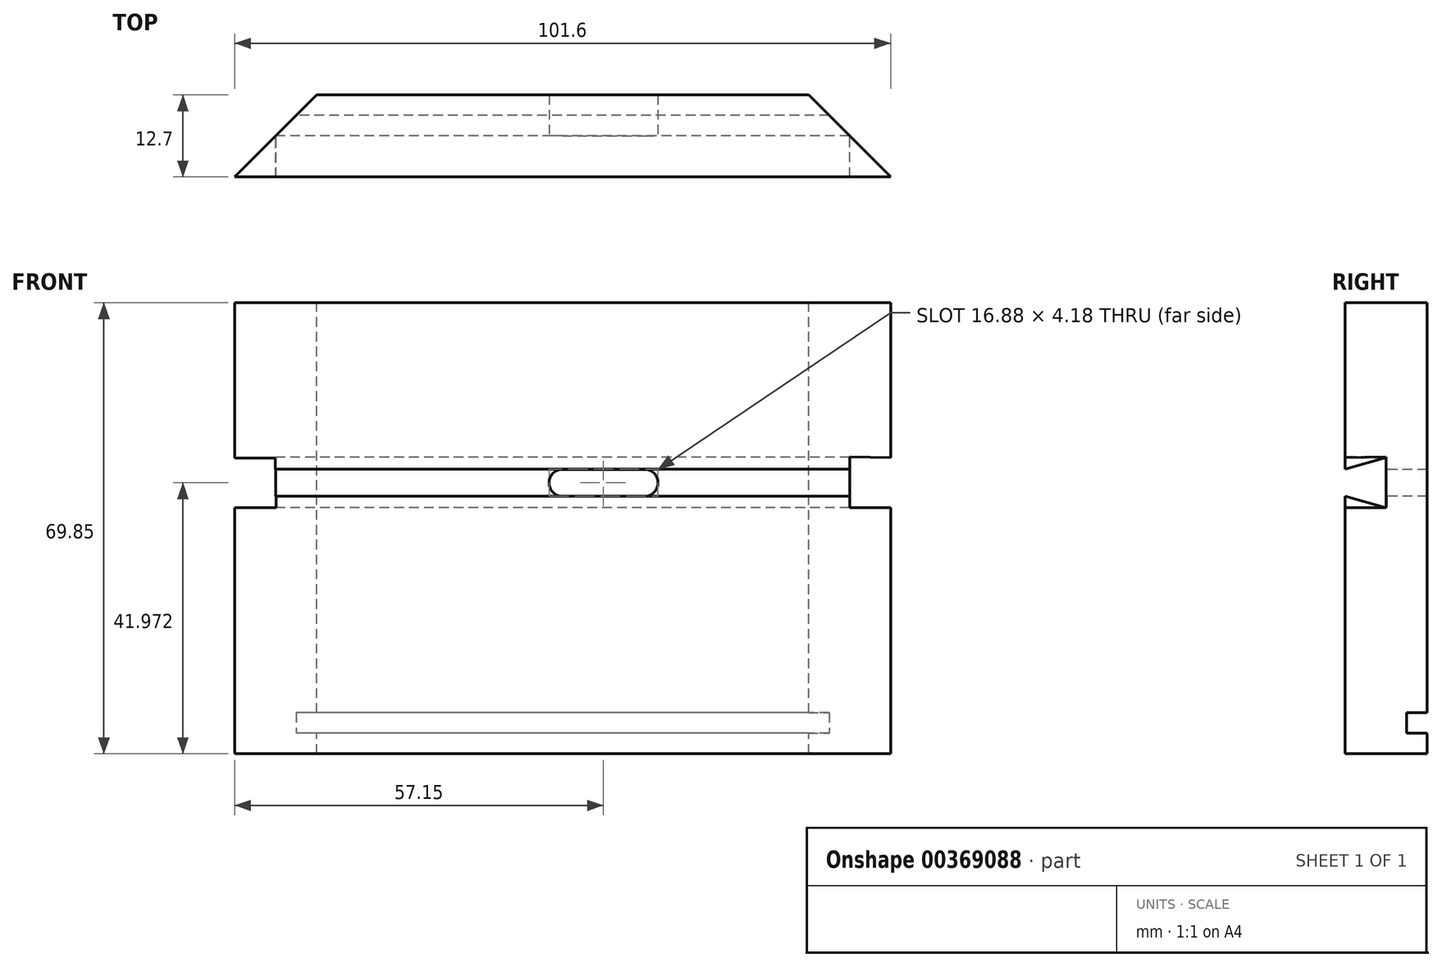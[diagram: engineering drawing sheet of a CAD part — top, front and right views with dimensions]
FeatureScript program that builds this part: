
annotation { "Feature Type Name" : "Feature", "Feature Type Description" : "" }
export const myFeature = defineFeature(function(context is Context, id is Id, definition is map)
    precondition{}
    {
        {
            var Q0;
            Q0=qCreatedBy(makeId("Front.planeOp"),FACE);
            var sketch = newSketch(context, id + "F0", { "sketchPlane" : qUnion([Q0])});
            skLineSegment(sketch, "E0.bottom", {"start": v(0, 0) * mm, "end": v(101.6, 0) * mm});
            skLineSegment(sketch, "E0.top", {"start": v(0, 76.2) * mm, "end": v(101.6, 76.2) * mm});
            skLineSegment(sketch, "E0.left", {"start": v(0, 0) * mm, "end": v(0, 76.2) * mm});
            skLineSegment(sketch, "E0.right", {"start": v(101.6, 0) * mm, "end": v(101.6, 76.2) * mm});
            skPoint(sketch, "E1.oppositeSnap0", {"position": v(0, 38.1) * mm});
            skLineSegment(sketch, "E1.bottom", {"start": v(0, 38.1) * mm, "end": v(-1.97, 38.1) * mm});
            skLineSegment(sketch, "E1.top", {"start": v(0, 38.1) * mm, "end": v(-1.97, 38.1) * mm});
            skLineSegment(sketch, "E1.left", {"start": v(0, 38.1) * mm, "end": v(0, 38.1) * mm});
            skLineSegment(sketch, "E1.right", {"start": v(-1.97, 38.1) * mm, "end": v(-1.97, 38.1) * mm});
            skSolve(sketch);
        }
        {
            var Q0;
            {var subQ3=sQuery(id+"F0.wireOp",EDGE,"E0.bottom");Q0=makeQuery(id+"F0.imprint","IMPRINT",FACE,{"disambiguationData":[TD([[makeQuery(id+"F0.imprint","IMPRINT",EDGE,{"derivedFrom":subQ3}),1.0]])]});}
            extrude(context, id + "F1", {"entities" : qUnion([Q0]), "endBound" : BoundingType.SYMMETRIC, "depth" : 12.7 * mm});
        }
        {
            var Q0;
            Q0=makeQuery(id+"F1.opExtrude","SWEPT_FACE",FACE,{"disambiguationData":[OSD([sQuery(id+"F0.wireOp",EDGE,"E0.left")])]});
            var sketch = newSketch(context, id + "F2", { "sketchPlane" : qUnion([Q0])});
            skLineSegment(sketch, "E2", {"start": v(0, 38.1) * mm, "end": v(0, 45.91) * mm});
            skLineSegment(sketch, "E3", {"start": v(0, 45.91) * mm, "end": v(6.35, 44.09) * mm, "construction": true});
            skLineSegment(sketch, "E4", {"start": v(6.35, 44.09) * mm, "end": v(6.35, 39.92) * mm});
            skLineSegment(sketch, "E5", {"start": v(0, 38.1) * mm, "end": v(6.35, 39.92) * mm});
            skPoint(sketch, "E6.orphan", {"position": v(6.35, 38.1) * mm});
            skPoint(sketch, "E7.end.orphan", {"position": v(-6.35, 38.1) * mm});
            skLineSegment(sketch, "E8", {"start": v(0, 45.91) * mm, "end": v(6.35, 44.09) * mm});
            skSolve(sketch);
        }
        {
            var Q0;
            Q0=qSketchRegion(id+"F2",true);
            extrude(context, id + "F3", {"entities" : qUnion([Q0]), "operationType" : NewBodyOperationType.REMOVE, "oppositeDirection" : true, "depth" : 279.4 * mm});
        }
        {
            var Q0;
            Q0=makeQuery(id+"F1.opExtrude","CAP_FACE",FACE,{"disambiguationData":[OSD([sQuery(id+"F0.wireOp",EDGE,"E0.bottom"),sQuery(id+"F0.wireOp",EDGE,"E0.top"),sQuery(id+"F0.wireOp",EDGE,"E0.left"),sQuery(id+"F0.wireOp",EDGE,"E0.right")])],"isStart":true});
            var sketch = newSketch(context, id + "F4", { "sketchPlane" : qUnion([Q0])});
            skLineSegment(sketch, "E9", {"start": v(-101.6, 73.03) * mm, "end": v(0, 73.03) * mm});
            skLineSegment(sketch, "E10", {"start": v(-101.6, 3.18) * mm, "end": v(0, 3.18) * mm});
            skLineSegment(sketch, "E11.0", {"start": v(-101.6, 69.85) * mm, "end": v(0, 69.85) * mm});
            skLineSegment(sketch, "E12.0", {"start": v(-101.6, 6.35) * mm, "end": v(0, 6.35) * mm});
            skSolve(sketch);
        }
        {
            var Q0;
            Q0=qSketchRegion(id+"F4",true);
            var Q1;
            {var subQ0=sQuery(id+"F4.wireOp",EDGE,"lRrMOG9n-2j56-arty-YlBW-zS80D7JPeCeS");Q1=makeQuery(id+"F4.imprint","IMPRINT",FACE,{"disambiguationData":[TD([[makeQuery(id+"F4.imprint","IMPRINT",EDGE,{"derivedFrom":subQ0}),1.0]])]});}
            var Q2;
            {var subQ0=sQuery(id+"F4.wireOp",EDGE,"RMjDy9hW-kbgy-mOy6-AWaG-f11VmHa6MSCS");var subQ1=sQuery(id+"F0.wireOp",EDGE,"E0.top");var subQ2=makeQuery(id+"FlYHEl8vpLPmmuw_1.boolean.opBoolean","COPY",EDGE,{"derivedFrom":makeQuery(id+"FlYHEl8vpLPmmuw_1.opExtrude","SWEPT_EDGE",EDGE,{"disambiguationData":[OSD([subQ1,sQuery(id+"Fw1e9hh29NmHN4y_1.wireOp",EDGE,"mT7uMHv0-vwrw-5TJk-CLzh-nBZqrL4YpAzT")])]})});var subQ3=makeQuery(id+"F4.imprint","INTERSECT",VERTEX,{"derivedFrom":[subQ2,subQ0]});Q2=makeQuery(id+"F4.imprint","IMPRINT",FACE,{"disambiguationData":[TD([[makeQuery(id+"F4.imprint","IMPRINT",EDGE,{"disambiguationData":[TD([[subQ3,1.0]])],"derivedFrom":subQ0}),1.0]])]});}
            var Q3;
            {var subQ0=sQuery(id+"F4.wireOp",EDGE,"E10");Q3=makeQuery(id+"F4.imprint","IMPRINT",FACE,{"disambiguationData":[TD([[makeQuery(id+"F4.imprint","IMPRINT",EDGE,{"derivedFrom":subQ0}),1.0]])]});}
            extrude(context, id + "F5", {"entities" : qUnion([Q0, Q1, Q2, Q3]), "operationType" : NewBodyOperationType.REMOVE, "oppositeDirection" : true, "depth" : 3.17 * mm});
        }
        {
            var Q0;
            Q0=makeQuery(id+"F3.boolean.opBoolean","COPY",FACE,{"derivedFrom":makeQuery(id+"F3.opExtrude","SWEPT_FACE",FACE,{"disambiguationData":[OSD([sQuery(id+"F2.wireOp",EDGE,"E2")])]})});
            var sketch = newSketch(context, id + "F6", { "sketchPlane" : qUnion([Q0])});
            skPoint(sketch, "E13.endSnap0", {"position": v(50.8, 45.91) * mm});
            skPoint(sketch, "E14.orphan", {"position": v(50.8, 55.4) * mm});
            skLineSegment(sketch, "E15", {"start": v(50.8, 44.06) * mm, "end": v(63.5, 44.06) * mm});
            skLineSegment(sketch, "E16", {"start": v(63.5, 44.06) * mm, "end": v(63.5, 39.88) * mm});
            skLineSegment(sketch, "E17", {"start": v(63.5, 39.88) * mm, "end": v(50.8, 39.88) * mm});
            skLineSegment(sketch, "E18", {"start": v(50.8, 39.88) * mm, "end": v(50.8, 44.06) * mm});
            skArc(sketch, "E19", {"start": v(50.8, 39.88) * mm, "mid": v(48.71, 41.97) * mm, "end": v(50.8, 44.06) * mm});
            skArc(sketch, "E20", {"start": v(63.5, 39.88) * mm, "mid": v(65.59, 41.97) * mm, "end": v(63.5, 44.06) * mm});
            skSolve(sketch);
        }
        {
            var Q0;
            Q0=makeQuery(id+"F6.imprint","IMPRINT",FACE,{"disambiguationData":[TD([[makeQuery(id+"F6.imprint","IMPRINT",EDGE,{"derivedFrom":sQuery(id+"F6.wireOp",EDGE,"E18")}),1.0]])]});
            var Q1;
            Q1=makeQuery(id+"F6.imprint","IMPRINT",FACE,{"disambiguationData":[TD([[makeQuery(id+"F6.imprint","IMPRINT",EDGE,{"derivedFrom":sQuery(id+"F6.wireOp",EDGE,"E15")}),-1.0]])]});
            var Q2;
            Q2=makeQuery(id+"F6.imprint","IMPRINT",FACE,{"disambiguationData":[TD([[makeQuery(id+"F6.imprint","IMPRINT",EDGE,{"derivedFrom":sQuery(id+"F6.wireOp",EDGE,"E16")}),1.0]])]});
            extrude(context, id + "F7", {"entities" : qUnion([Q0, Q1, Q2]), "operationType" : NewBodyOperationType.REMOVE, "oppositeDirection" : true, "depth" : 25.4 * mm});
        }
        {
            var Q0;
            {var subQ0=sQuery(id+"F0.wireOp",EDGE,"E0.top");var subQ1=sQuery(id+"F0.wireOp",EDGE,"E0.left");var subQ2=sQuery(id+"F0.wireOp",EDGE,"E0.right");Q0=makeQuery(id+"F3.boolean.opBoolean","SPLIT",FACE,{"disambiguationData":[TD([makeQuery(id+"F1.opExtrude","SWEPT_FACE",FACE,{"disambiguationData":[OSD([subQ0])]})])],"derivedFrom":makeQuery(id+"F1.opExtrude","CAP_FACE",FACE,{"disambiguationData":[OSD([sQuery(id+"F0.wireOp",EDGE,"E0.bottom"),subQ0,subQ1,subQ2])],"isStart":false})});}
            var sketch = newSketch(context, id + "F8", { "sketchPlane" : qUnion([Q0])});
            skLineSegment(sketch, "E21", {"start": v(0, 69.85) * mm, "end": v(101.6, 69.85) * mm});
            skSolve(sketch);
        }
        {
            var Q0;
            {var subQ0=sQuery(id+"F8.wireOp",EDGE,"E21");Q0=makeQuery(id+"F8.imprint","IMPRINT",FACE,{"disambiguationData":[TD([[makeQuery(id+"F8.imprint","IMPRINT",EDGE,{"derivedFrom":subQ0}),1.0]])]});}
            extrude(context, id + "F9", {"entities" : qUnion([Q0]), "operationType" : NewBodyOperationType.REMOVE, "oppositeDirection" : true, "depth" : 25.4 * mm});
        }
        {
            var Q0;
            Q0=makeQuery(id+"F9.boolean.opBoolean","COPY",FACE,{"derivedFrom":makeQuery(id+"F9.opExtrude","SWEPT_FACE",FACE,{"disambiguationData":[OSD([sQuery(id+"F8.wireOp",EDGE,"E21")])]})});
            var sketch = newSketch(context, id + "F10", { "sketchPlane" : qUnion([Q0])});
            skLineSegment(sketch, "E22", {"start": v(0, -6.35) * mm, "end": v(12.7, 6.35) * mm});
            skLineSegment(sketch, "E23", {"start": v(101.6, -6.35) * mm, "end": v(88.9, 6.35) * mm});
            skSolve(sketch);
        }
        {
            var Q0;
            Q0 = qSketchRegion(id + "F10", true);
            var Q1;
            {var subQ0=sQuery(id+"F10.wireOp",EDGE,"E22");Q1=makeQuery(id+"F10.imprint","IMPRINT",FACE,{"disambiguationData":[TD([[makeQuery(id+"F10.imprint","IMPRINT",EDGE,{"derivedFrom":subQ0}),1.0]])]});}
            var Q2;
            {var subQ0=sQuery(id+"F10.wireOp",EDGE,"E23");Q2=makeQuery(id+"F10.imprint","IMPRINT",FACE,{"disambiguationData":[TD([[makeQuery(id+"F10.imprint","IMPRINT",EDGE,{"derivedFrom":subQ0}),-1.0]])]});}
            extrude(context, id + "F11", {"entities" : qUnion([Q0, Q1, Q2]), "operationType" : NewBodyOperationType.REMOVE, "endBound" : BoundingType.THROUGH_ALL, "oppositeDirection" : true, "depth" : 25.4 * mm});
        }
        {
            var Q0;
            {var subQ0=sQuery(id+"F0.wireOp",EDGE,"E0.top");var subQ1=sQuery(id+"F0.wireOp",EDGE,"E0.left");var subQ2=sQuery(id+"F0.wireOp",EDGE,"E0.right");Q0=makeQuery(id+"F3.boolean.opBoolean","SPLIT",FACE,{"disambiguationData":[TD([makeQuery(id+"F1.opExtrude","SWEPT_FACE",FACE,{"disambiguationData":[OSD([subQ0])]})])],"derivedFrom":makeQuery(id+"F1.opExtrude","CAP_FACE",FACE,{"disambiguationData":[OSD([sQuery(id+"F0.wireOp",EDGE,"E0.bottom"),subQ0,subQ1,subQ2])],"isStart":false})});}
            var sketch = newSketch(context, id + "F12", { "sketchPlane" : qUnion([Q0])});
            skLineSegment(sketch, "E24", {"start": v(95.3, 45.97) * mm, "end": v(95.3, 38.1) * mm});
            skLineSegment(sketch, "E25", {"start": v(95.3, 38.1) * mm, "end": v(101.6, 38.1) * mm});
            skLineSegment(sketch, "E26", {"start": v(101.6, 38.1) * mm, "end": v(101.6, 45.87) * mm});
            skLineSegment(sketch, "E27", {"start": v(101.6, 45.87) * mm, "end": v(95.3, 45.97) * mm});
            skSolve(sketch);
        }
        {
            var Q0;
            {var subQ0=sQuery(id+"F12.wireOp",EDGE,"E25");Q0=makeQuery(id+"F12.imprint","IMPRINT",FACE,{"disambiguationData":[TD([[makeQuery(id+"F12.imprint","IMPRINT",EDGE,{"derivedFrom":subQ0}),1.0]])]});}
            var Q1;
            {var subQ0=sQuery(id+"F12.wireOp",EDGE,"E27");Q1=makeQuery(id+"F12.imprint","IMPRINT",FACE,{"disambiguationData":[TD([[makeQuery(id+"F12.imprint","IMPRINT",EDGE,{"derivedFrom":subQ0}),1.0]])]});}
            extrude(context, id + "F13", {"entities" : qUnion([Q0, Q1]), "operationType" : NewBodyOperationType.REMOVE, "oppositeDirection" : true, "depth" : 6.35 * mm});
        }
        {
            var Q0;
            {var subQ0=sQuery(id+"F0.wireOp",EDGE,"E0.bottom");var subQ1=sQuery(id+"F0.wireOp",EDGE,"E0.right");var subQ2=sQuery(id+"F0.wireOp",EDGE,"E0.left");Q0=makeQuery(id+"F3.boolean.opBoolean","SPLIT",FACE,{"disambiguationData":[TD([makeQuery(id+"F1.opExtrude","SWEPT_FACE",FACE,{"disambiguationData":[OSD([subQ0])]})])],"derivedFrom":makeQuery(id+"F1.opExtrude","CAP_FACE",FACE,{"disambiguationData":[OSD([subQ0,sQuery(id+"F0.wireOp",EDGE,"E0.top"),subQ2,subQ1])],"isStart":false})});}
            var sketch = newSketch(context, id + "F14", { "sketchPlane" : qUnion([Q0])});
            skLineSegment(sketch, "E28", {"start": v(6.44, 39.92) * mm, "end": v(6.44, 38.11) * mm});
            skLineSegment(sketch, "E29", {"start": v(6.44, 38.11) * mm, "end": v(0, 38.11) * mm});
            skLineSegment(sketch, "E30", {"start": v(0, 38.11) * mm, "end": v(0, 45.94) * mm});
            skLineSegment(sketch, "E31", {"start": v(0, 45.94) * mm, "end": v(6.44, 45.94) * mm});
            skLineSegment(sketch, "E32", {"start": v(6.44, 45.94) * mm, "end": v(6.44, 39.92) * mm});
            skSolve(sketch);
        }
        {
            var Q0;
            {var subQ0=sQuery(id+"F14.wireOp",EDGE,"E28");Q0=makeQuery(id+"F14.imprint","IMPRINT",FACE,{"disambiguationData":[TD([[makeQuery(id+"F14.imprint","IMPRINT",EDGE,{"derivedFrom":subQ0}),-1.0]])]});}
            extrude(context, id + "F15", {"entities" : qUnion([Q0]), "operationType" : NewBodyOperationType.REMOVE, "oppositeDirection" : true, "depth" : 25.4 * mm});
        }
        {
            var Q0;
            {var subQ0=sQuery(id+"F0.wireOp",EDGE,"E0.top");var subQ1=sQuery(id+"F0.wireOp",EDGE,"E0.left");var subQ2=sQuery(id+"F0.wireOp",EDGE,"E0.right");Q0=makeQuery(id+"F3.boolean.opBoolean","SPLIT",FACE,{"disambiguationData":[TD([makeQuery(id+"F1.opExtrude","SWEPT_FACE",FACE,{"disambiguationData":[OSD([subQ0])]})])],"derivedFrom":makeQuery(id+"F1.opExtrude","CAP_FACE",FACE,{"disambiguationData":[OSD([sQuery(id+"F0.wireOp",EDGE,"E0.bottom"),subQ0,subQ1,subQ2])],"isStart":false})});}
            var sketch = newSketch(context, id + "F16", { "sketchPlane" : qUnion([Q0])});
            skLineSegment(sketch, "E33", {"start": v(6.35, 44.09) * mm, "end": v(6.35, 45.8) * mm});
            skLineSegment(sketch, "E34", {"start": v(6.35, 45.8) * mm, "end": v(0, 45.8) * mm});
            skSolve(sketch);
        }
        {
            var Q0;
            Q0 = qSketchRegion(id + "F16", true);
            var Q1;
            {var subQ0=sQuery(id+"F16.wireOp",EDGE,"E33");Q1=makeQuery(id+"F16.imprint","IMPRINT",FACE,{"disambiguationData":[TD([[makeQuery(id+"F16.imprint","IMPRINT",EDGE,{"derivedFrom":subQ0}),1.0]])]});}
            extrude(context, id + "F17", {"entities" : qUnion([Q0, Q1]), "operationType" : NewBodyOperationType.REMOVE, "oppositeDirection" : true, "depth" : 25.4 * mm});
        }
    });
